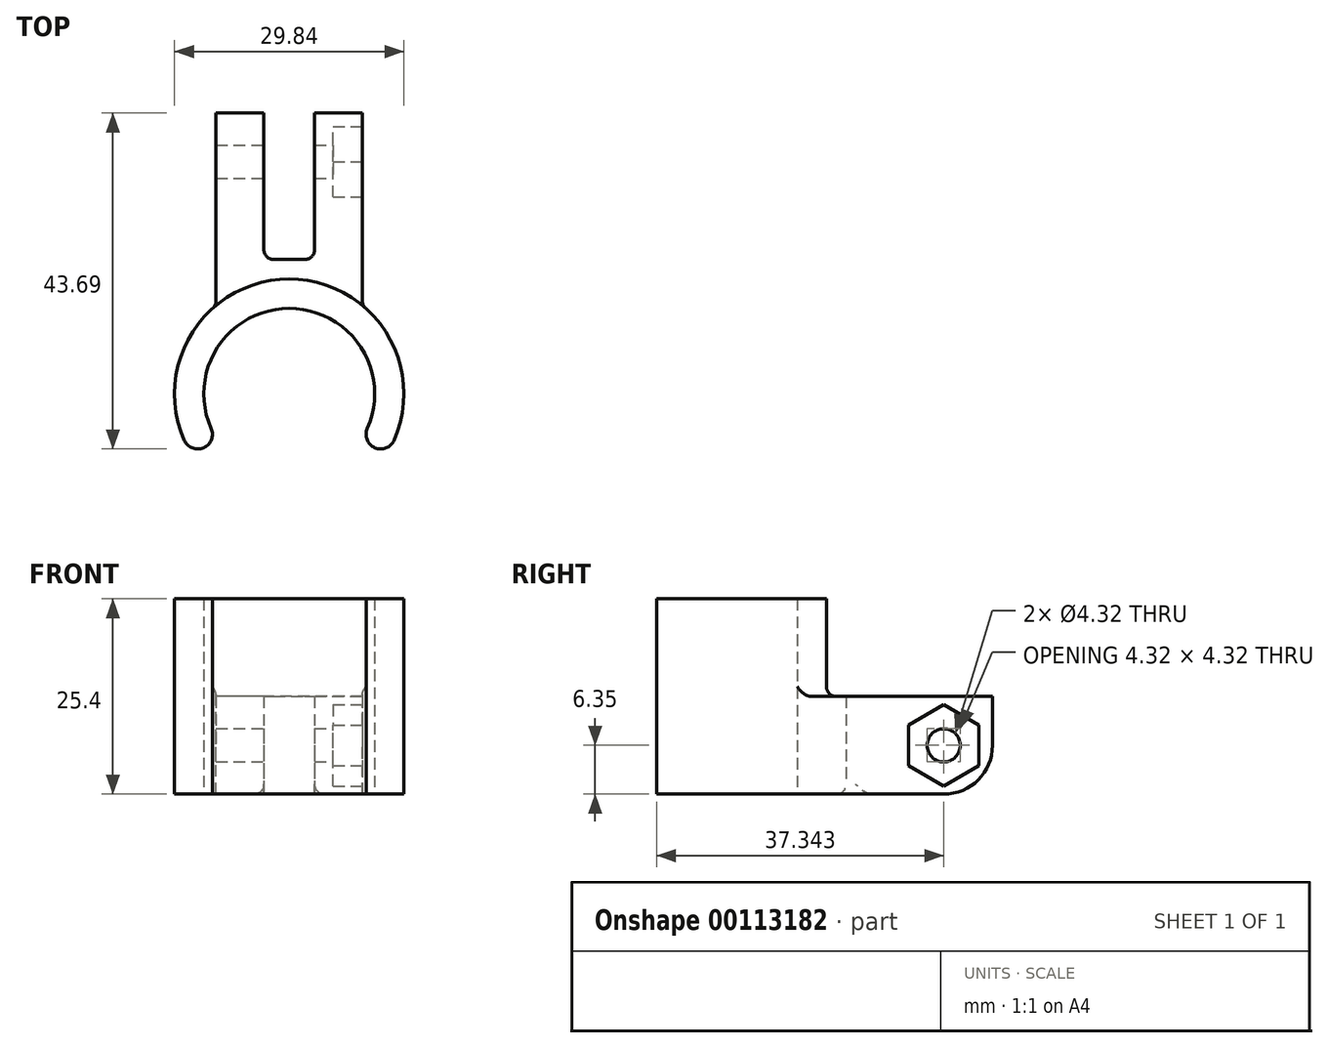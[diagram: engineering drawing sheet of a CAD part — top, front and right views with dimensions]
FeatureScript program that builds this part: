
annotation { "Feature Type Name" : "Feature", "Feature Type Description" : "" }
export const myFeature = defineFeature(function(context is Context, id is Id, definition is map)
    precondition{}
    {
        {
            var Q0;
            Q0=qCreatedBy(makeId("Top.planeOp"),FACE);
            var sketch = newSketch(context, id + "F0", { "sketchPlane" : qUnion([Q0])});
            skArc(sketch, "E0", {"start": v(-10.16, -4.5) * mm, "mid": v(0, -11.11) * mm, "end": v(10.16, -4.5) * mm, "construction": true});
            skArc(sketch, "E1", {"start": v(10.16, -4.5) * mm, "mid": v(0, 11.11) * mm, "end": v(-10.16, -4.5) * mm});
            skLineSegment(sketch, "E2", {"start": v(-3.3, 17.46) * mm, "end": v(3.3, 17.46) * mm});
            skPoint(sketch, "E3", {"position": v(0, 17.46) * mm});
            skArc(sketch, "E4", {"start": v(-13.64, -6.04) * mm, "mid": v(-11.13, -7.01) * mm, "end": v(-10.16, -4.5) * mm});
            skLineSegment(sketch, "E5", {"start": v(-10.16, -4.5) * mm, "end": v(-13.64, -6.04) * mm, "construction": true});
            skLineSegment(sketch, "E6", {"start": v(-3.3, 17.46) * mm, "end": v(-3.3, 36.51) * mm});
            skLineSegment(sketch, "E7", {"start": v(3.3, 17.46) * mm, "end": v(3.3, 36.51) * mm});
            skLineSegment(sketch, "E8", {"start": v(-3.3, 36.51) * mm, "end": v(-9.53, 36.51) * mm});
            skLineSegment(sketch, "E9", {"start": v(3.3, 36.51) * mm, "end": v(9.52, 36.51) * mm});
            skLineSegment(sketch, "E10", {"start": v(-9.53, 36.51) * mm, "end": v(-9.53, 11.49) * mm});
            skLineSegment(sketch, "E11", {"start": v(9.53, 36.51) * mm, "end": v(9.53, 11.49) * mm});
            skLineSegment(sketch, "E12", {"start": v(-9.53, 11.49) * mm, "end": v(-7.1, 8.55) * mm, "construction": true});
            skLineSegment(sketch, "E13", {"start": v(9.53, 11.49) * mm, "end": v(7.1, 8.55) * mm, "construction": true});
            skArc(sketch, "E14", {"start": v(10.16, -4.5) * mm, "mid": v(11.13, -7.01) * mm, "end": v(13.64, -6.04) * mm});
            skLineSegment(sketch, "E15", {"start": v(13.64, -6.04) * mm, "end": v(10.16, -4.5) * mm, "construction": true});
            skArc(sketch, "E16", {"start": v(-9.52, 11.49) * mm, "mid": v(-14.53, 3.41) * mm, "end": v(-13.64, -6.04) * mm});
            skArc(sketch, "E17", {"start": v(13.64, -6.04) * mm, "mid": v(14.53, 3.41) * mm, "end": v(9.53, 11.49) * mm});
            skSolve(sketch);
        }
        {
            var Q0;
            Q0 = qSketchRegion(id + "F0", true);
            extrude(context, id + "F1", {"entities" : qUnion([Q0]), "depth" : 25.4 * mm});
        }
        {
            var Q0;
            Q0=makeQuery(id+"F1.opExtrude","SWEPT_FACE",FACE,{"disambiguationData":[OSD([sQuery(id+"F0.wireOp",EDGE,"E11")])]});
            var sketch = newSketch(context, id + "F2", { "sketchPlane" : qUnion([Q0])});
            skCircle(sketch, "E18", {"center": v(30.16, 6.35) * mm, "radius": 2.16 * mm});
            skSolve(sketch);
        }
        {
            var Q0;
            Q0 = qSketchRegion(id + "F2", true);
            var Q1;
            Q1=makeQuery(id+"F1.opExtrude","SWEPT_FACE",FACE,{"disambiguationData":[OSD([sQuery(id+"F0.wireOp",EDGE,"E10")])]});
            extrude(context, id + "F3", {"entities" : qUnion([Q0]), "operationType" : NewBodyOperationType.REMOVE, "endBound" : BoundingType.UP_TO_SURFACE, "oppositeDirection" : true, "endBoundEntityFace" : qUnion([Q1]), "depth" : 25.4 * mm});
        }
        {
            var Q0;
            Q0=makeQuery(id+"F1.opExtrude","SWEPT_FACE",FACE,{"disambiguationData":[OSD([sQuery(id+"F0.wireOp",EDGE,"E11")])]});
            var sketch = newSketch(context, id + "F4", { "sketchPlane" : qUnion([Q0])});
            skCircle(sketch, "E19.cCircle", {"center": v(30.16, 6.35) * mm, "radius": 4.57 * mm, "construction": true});
            skLineSegment(sketch, "E19.0", {"start": v(30.16, 11.63) * mm, "end": v(34.73, 8.99) * mm});
            skLineSegment(sketch, "E19.1", {"start": v(34.73, 8.99) * mm, "end": v(34.73, 3.71) * mm});
            skLineSegment(sketch, "E19.2", {"start": v(34.73, 3.71) * mm, "end": v(30.16, 1.07) * mm});
            skLineSegment(sketch, "E19.3", {"start": v(30.16, 1.07) * mm, "end": v(25.6, 3.71) * mm});
            skLineSegment(sketch, "E19.4", {"start": v(25.6, 3.71) * mm, "end": v(25.6, 8.99) * mm});
            skLineSegment(sketch, "E19.5", {"start": v(25.6, 8.99) * mm, "end": v(30.16, 11.63) * mm});
            skPoint(sketch, "E19.0.midPoint", {"position": v(32.45, 10.3) * mm});
            skSolve(sketch);
        }
        {
            var Q0;
            Q0 = qSketchRegion(id + "F4", true);
            extrude(context, id + "F5", {"entities" : qUnion([Q0]), "operationType" : NewBodyOperationType.REMOVE, "oppositeDirection" : true, "depth" : 3.8 * mm});
        }
        {
            var Q0;
            Q0=makeQuery(id+"F1.opExtrude","CAP_FACE",FACE,{"disambiguationData":[OSD([sQuery(id+"F0.wireOp",EDGE,"E1"),sQuery(id+"F0.wireOp",EDGE,"E2"),sQuery(id+"F0.wireOp",EDGE,"E4"),sQuery(id+"F0.wireOp",EDGE,"E6"),sQuery(id+"F0.wireOp",EDGE,"E7"),sQuery(id+"F0.wireOp",EDGE,"E8"),sQuery(id+"F0.wireOp",EDGE,"E9"),sQuery(id+"F0.wireOp",EDGE,"E10"),sQuery(id+"F0.wireOp",EDGE,"E11"),sQuery(id+"F0.wireOp",EDGE,"E14"),sQuery(id+"F0.wireOp",EDGE,"E16"),sQuery(id+"F0.wireOp",EDGE,"E17")])],"isStart":false});
            var sketch = newSketch(context, id + "F6", { "sketchPlane" : qUnion([Q0])});
            skLineSegment(sketch, "E20", {"start": v(-9.52, 11.49) * mm, "end": v(-9.53, 36.51) * mm});
            skLineSegment(sketch, "E21", {"start": v(-9.53, 36.51) * mm, "end": v(-3.3, 36.51) * mm});
            skLineSegment(sketch, "E22", {"start": v(-3.3, 36.51) * mm, "end": v(-3.3, 17.46) * mm});
            skLineSegment(sketch, "E23", {"start": v(-3.3, 17.46) * mm, "end": v(3.3, 17.46) * mm});
            skLineSegment(sketch, "E24", {"start": v(3.3, 17.46) * mm, "end": v(3.3, 36.51) * mm});
            skLineSegment(sketch, "E25", {"start": v(3.3, 36.51) * mm, "end": v(9.53, 36.51) * mm});
            skLineSegment(sketch, "E26", {"start": v(9.53, 36.51) * mm, "end": v(9.53, 11.49) * mm});
            skArc(sketch, "E27", {"start": v(9.53, 11.49) * mm, "mid": v(0, 14.92) * mm, "end": v(-9.52, 11.49) * mm});
            skSolve(sketch);
        }
        {
            var Q0;
            Q0 = qSketchRegion(id + "F6", true);
            extrude(context, id + "F7", {"entities" : qUnion([Q0]), "operationType" : NewBodyOperationType.REMOVE, "oppositeDirection" : true, "depth" : 12.7 * mm});
        }
        {
            var Q0;
            Q0=makeQuery(id+"F1.opExtrude","CAP_EDGE",EDGE,{"disambiguationData":[OSD([sQuery(id+"F0.wireOp",EDGE,"E9")])],"isStart":true});
            var Q1;
            Q1=makeQuery(id+"F1.opExtrude","CAP_EDGE",EDGE,{"disambiguationData":[OSD([sQuery(id+"F0.wireOp",EDGE,"E8")])],"isStart":true});
            var Q2;
            Q2=makeQuery(id+"F7.boolean.opBoolean","COPY",EDGE,{"derivedFrom":makeQuery(id+"F7.opExtrude","CAP_EDGE",EDGE,{"disambiguationData":[OSD([sQuery(id+"F6.wireOp",EDGE,"E21")])],"isStart":false})});
            var Q3;
            Q3=makeQuery(id+"F7.boolean.opBoolean","COPY",EDGE,{"derivedFrom":makeQuery(id+"F7.opExtrude","CAP_EDGE",EDGE,{"disambiguationData":[OSD([sQuery(id+"F6.wireOp",EDGE,"E25")])],"isStart":false})});
            fillet(context, id + "F8", {"entities" : qUnion([Q0, Q1, Q2, Q3]), "radius" : 6.35 * mm, "tangentPropagation" : true, "allowEdgeOverflow" : false});
        }
        {
            var Q0;
            Q0=makeQuery(id+"F7.boolean.opBoolean","COPY",EDGE,{"derivedFrom":makeQuery(id+"F7.opExtrude","CAP_EDGE",EDGE,{"disambiguationData":[OSD([sQuery(id+"F6.wireOp",EDGE,"E27")])],"isStart":false})});
            var Q1;
            Q1=makeQuery(id+"F1.opExtrude","SWEPT_EDGE",EDGE,{"disambiguationData":[OSD([sQuery(id+"F0.wireOp",EDGE,"E11"),sQuery(id+"F0.wireOp",EDGE,"E17")])]});
            var Q2;
            Q2=makeQuery(id+"F1.opExtrude","SWEPT_EDGE",EDGE,{"disambiguationData":[OSD([sQuery(id+"F0.wireOp",EDGE,"E10"),sQuery(id+"F0.wireOp",EDGE,"E16")])]});
            var Q3;
            Q3=makeQuery(id+"F7.boolean.opBoolean","MERGE",EDGE,{"derivedFrom":[makeQuery(id+"F1.opExtrude","CAP_EDGE",EDGE,{"disambiguationData":[OSD([sQuery(id+"F0.wireOp",EDGE,"E16")])],"isStart":false}),makeQuery(id+"F1.opExtrude","CAP_EDGE",EDGE,{"disambiguationData":[OSD([sQuery(id+"F0.wireOp",EDGE,"E17")])],"isStart":false}),makeQuery(id+"F7.opExtrude","CAP_EDGE",EDGE,{"disambiguationData":[OSD([sQuery(id+"F6.wireOp",EDGE,"E27")])],"isStart":true})]});
            fillet(context, id + "F9", {"entities" : qUnion([Q0, Q1, Q2, Q3]), "radius" : 1.27 * mm, "tangentPropagation" : true, "allowEdgeOverflow" : false});
        }
        {
            var Q0;
            Q0=makeQuery(id+"F7.boolean.opBoolean","COPY",EDGE,{"derivedFrom":makeQuery(id+"F7.opExtrude","CAP_EDGE",EDGE,{"disambiguationData":[OSD([sQuery(id+"F6.wireOp",EDGE,"E26")])],"isStart":false})});
            var Q1;
            Q1=makeQuery(id+"F1.opExtrude","CAP_EDGE",EDGE,{"disambiguationData":[OSD([sQuery(id+"F0.wireOp",EDGE,"E2")])],"isStart":true});
            var Q2;
            Q2=makeQuery(id+"F1.opExtrude","SWEPT_EDGE",EDGE,{"disambiguationData":[OSD([sQuery(id+"F0.wireOp",EDGE,"E2"),sQuery(id+"F0.wireOp",EDGE,"E7")])]});
            var Q3;
            Q3=makeQuery(id+"F1.opExtrude","SWEPT_EDGE",EDGE,{"disambiguationData":[OSD([sQuery(id+"F0.wireOp",EDGE,"E2"),sQuery(id+"F0.wireOp",EDGE,"E6")])]});
            fillet(context, id + "F10", {"entities" : qUnion([Q0, Q1, Q2, Q3]), "radius" : 1.27 * mm, "tangentPropagation" : true, "allowEdgeOverflow" : false});
        }
    });
